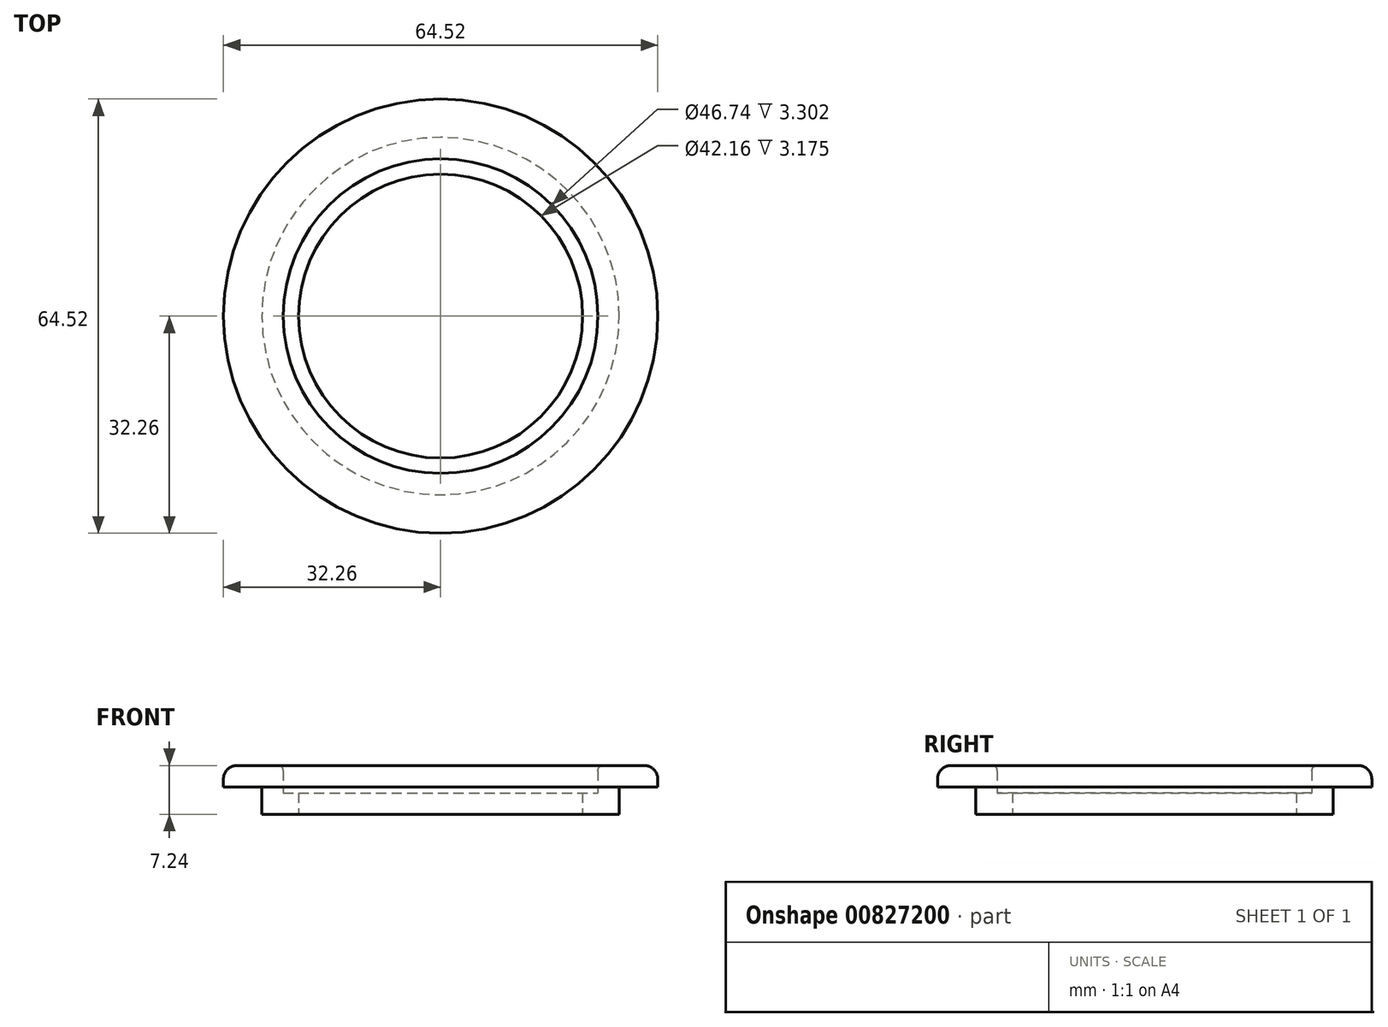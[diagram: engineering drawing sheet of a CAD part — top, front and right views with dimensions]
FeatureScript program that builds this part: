
annotation { "Feature Type Name" : "Feature", "Feature Type Description" : "" }
export const myFeature = defineFeature(function(context is Context, id is Id, definition is map)
    precondition{}
    {
        {
            var Q0;
            Q0=qCreatedBy(makeId("Right.planeOp"),FACE);
            var sketch = newSketch(context, id + "F0", { "sketchPlane" : qUnion([Q0])});
            skLineSegment(sketch, "E0", {"start": v(21.08, 0) * mm, "end": v(23.37, 0) * mm});
            skLineSegment(sketch, "E1", {"start": v(23.37, 0) * mm, "end": v(23.37, 3.3) * mm});
            skLineSegment(sketch, "E2", {"start": v(24.13, 4.06) * mm, "end": v(30.23, 4.06) * mm});
            skPoint(sketch, "E3.orphan", {"position": v(0, 0) * mm});
            skLineSegment(sketch, "E4.0", {"start": v(26.54, 0.89) * mm, "end": v(32.26, 0.89) * mm});
            skLineSegment(sketch, "E4.1", {"start": v(26.54, -3.18) * mm, "end": v(26.54, 0.89) * mm});
            skLineSegment(sketch, "E4.2", {"start": v(21.08, -3.18) * mm, "end": v(26.54, -3.18) * mm});
            skLineSegment(sketch, "E5", {"start": v(32.26, 2.03) * mm, "end": v(32.26, 0.89) * mm});
            skLineSegment(sketch, "E6", {"start": v(21.08, 0) * mm, "end": v(21.08, -3.18) * mm});
            skPoint(sketch, "E7.visualSharp", {"position": v(32.26, 4.06) * mm});
            skArc(sketch, "E7.filletArc", {"start": v(32.26, 2.03) * mm, "mid": v(31.66, 3.47) * mm, "end": v(30.23, 4.06) * mm});
            skPoint(sketch, "E8.visualSharp", {"position": v(23.37, 4.06) * mm});
            skArc(sketch, "E8.filletArc", {"start": v(24.13, 4.06) * mm, "mid": v(23.6, 3.84) * mm, "end": v(23.37, 3.3) * mm});
            skLineSegment(sketch, "E9", {"start": v(0, 0) * mm, "end": v(0, 10.69) * mm});
            skSolve(sketch);
        }
        {
            var Q0;
            Q0=makeQuery(id+"F0.imprint","IMPRINT",FACE,{"disambiguationData":[TD([[makeQuery(id+"F0.imprint","IMPRINT",EDGE,{"derivedFrom":sQuery(id+"F0.wireOp",EDGE,"E0")}),-1.0]])]});
            var Q1;
            Q1=sQuery(id+"F0.wireOp",EDGE,"E9");
            revolve(context, id + "F1", {"surfaceOperationType" : NewSurfaceOperationType.NEW, "entities" : qUnion([Q0]), "axis" : qUnion([Q1]), "revolveType" : RevolveType.FULL});
        }
    });
